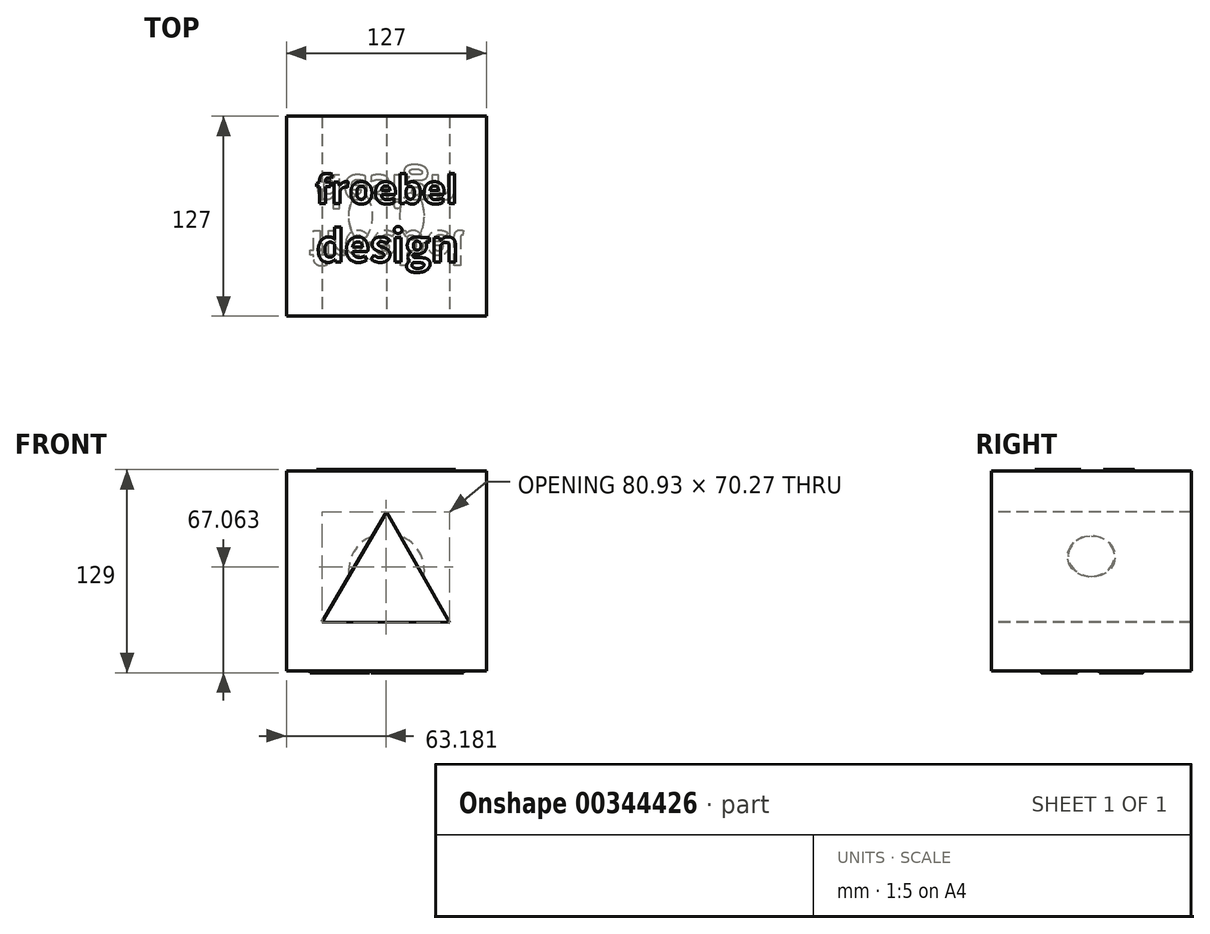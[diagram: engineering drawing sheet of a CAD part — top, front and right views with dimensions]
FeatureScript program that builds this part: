
annotation { "Feature Type Name" : "Feature", "Feature Type Description" : "" }
export const myFeature = defineFeature(function(context is Context, id is Id, definition is map)
    precondition{}
    {
        {
            var Q0;
            Q0=qCreatedBy(makeId("Top.planeOp"),FACE);
            var sketch = newSketch(context, id + "F0", { "sketchPlane" : qUnion([Q0])});
            skLineSegment(sketch, "E0.bottom", {"start": v(63.5, -63.5) * mm, "end": v(-63.5, -63.5) * mm});
            skLineSegment(sketch, "E0.top", {"start": v(63.5, 63.5) * mm, "end": v(-63.5, 63.5) * mm});
            skLineSegment(sketch, "E0.left", {"start": v(63.5, -63.5) * mm, "end": v(63.5, 63.5) * mm});
            skLineSegment(sketch, "E0.right", {"start": v(-63.5, -63.5) * mm, "end": v(-63.5, 63.5) * mm});
            skPoint(sketch, "E0.middle", {"position": v(0, 0) * mm});
            skSolve(sketch);
        }
        {
            var Q0;
            Q0 = qSketchRegion(id + "F0", true);
            extrude(context, id + "F1", {"entities" : qUnion([Q0]), "depth" : 63.5 * mm, "hasSecondDirection" : true, "secondDirectionOppositeDirection" : true, "secondDirectionDepth" : 63.5 * mm});
        }
        {
            var Q0;
            Q0=qCreatedBy(makeId("Front.planeOp"),FACE);
            var sketch = newSketch(context, id + "F2", { "sketchPlane" : qUnion([Q0])});
            skArc(sketch, "E1", {"start": v(0, 24.07) * mm, "mid": v(24.07, 0) * mm, "end": v(0, -24.07) * mm});
            skLineSegment(sketch, "E2", {"start": v(0, -24.07) * mm, "end": v(0, 24.07) * mm});
            skSolve(sketch);
        }
        {
            var Q0;
            Q0 = qSketchRegion(id + "F2", true);
            var Q1;
            Q1=sQuery(id+"F2.wireOp",EDGE,"E2");
            revolve(context, id + "F3", {"entities" : qUnion([Q0]), "axis" : qUnion([Q1]), "revolveType" : RevolveType.FULL});
        }
        {
            var Q0;
            Q0=makeQuery(id+"F1.opExtrude","SWEPT_FACE",FACE,{"disambiguationData":[OSD([sQuery(id+"F0.wireOp",EDGE,"E0.bottom")])]});
            var sketch = newSketch(context, id + "F4", { "sketchPlane" : qUnion([Q0])});
            skCircle(sketch, "E3.cCircle", {"center": v(-0.21, -9.03) * mm, "radius": 23.36 * mm, "construction": true});
            skLineSegment(sketch, "E3.0", {"start": v(0, 37.7) * mm, "end": v(40.15, -32.57) * mm});
            skLineSegment(sketch, "E3.1", {"start": v(40.15, -32.57) * mm, "end": v(-40.78, -32.2) * mm});
            skLineSegment(sketch, "E3.2", {"start": v(-40.78, -32.2) * mm, "end": v(0, 37.7) * mm});
            skPoint(sketch, "E3.0.midPoint", {"position": v(20.07, 2.56) * mm});
            skSolve(sketch);
        }
        {
            var Q0;
            Q0=makeQuery(id+"F4.imprint","IMPRINT",FACE,{"disambiguationData":[TD([[makeQuery(id+"F4.imprint","IMPRINT",EDGE,{"derivedFrom":sQuery(id+"F4.wireOp",EDGE,"E3.0")}),-1.0]])]});
            extrude(context, id + "F5", {"entities" : qUnion([Q0]), "operationType" : NewBodyOperationType.REMOVE, "endBound" : BoundingType.THROUGH_ALL, "oppositeDirection" : true, "depth" : 25.4 * mm});
        }
        {
            var Q0;
            Q0=qCreatedBy(makeId("Front.planeOp"),FACE);
            var sketch = newSketch(context, id + "F6", { "sketchPlane" : qUnion([Q0])});
            skLineSegment(sketch, "E4", {"start": v(0, 61.7) * mm, "end": v(0, -90.48) * mm});
            skSolve(sketch);
        }
        {
            var Q0;
            Q0=qCreatedBy(makeId("Front.planeOp"),FACE);
            var sketch = newSketch(context, id + "F7", { "sketchPlane" : qUnion([Q0])});
            skLineSegment(sketch, "E5", {"start": v(0, 0) * mm, "end": v(0, 95.52) * mm});
            skSolve(sketch);
        }
        {
            var Q0;
            Q0=makeQuery(id+"F1.opExtrude","CAP_FACE",FACE,{"disambiguationData":[OSD([sQuery(id+"F0.wireOp",EDGE,"E0.bottom"),sQuery(id+"F0.wireOp",EDGE,"E0.top"),sQuery(id+"F0.wireOp",EDGE,"E0.left"),sQuery(id+"F0.wireOp",EDGE,"E0.right")])],"isStart":false});
            var sketch = newSketch(context, id + "F8", { "sketchPlane" : qUnion([Q0])});
            skText(sketch, "E6", { "text": "froebel", "fontName": "OpenSans-Bold.ttf"});
            const initialGuessF8  = {"E6": [-0.045, 0.0079, 1, 0, 0.01817]};
            skSetInitialGuess(sketch, initialGuessF8);
            skSolve(sketch);
        }
        {
            var Q0;
            Q0=makeQuery(id+"F8.imprint","IMPRINT",FACE,{"disambiguationData":[TD([[makeQuery(id+"F8.imprint","IMPRINT",EDGE,{"derivedFrom":sQuery(id+"F8.wireOp",EDGE,"E6.sketch_text.stroke-0")}),1.0]])]});
            var sketch = newSketch(context, id + "F9", { "sketchPlane" : qUnion([Q0])});
            skText(sketch, "E7", { "text": "design", "fontName": "NotoSansCJKsc-Bold.otf"});
            const initialGuessF9  = {"E7": [-0.04464, -0.02906, 1, 0, 0.02]};
            skSetInitialGuess(sketch, initialGuessF9);
            skSolve(sketch);
        }
        {
            var Q0;
            Q0=makeQuery(id+"F1.opExtrude","CAP_FACE",FACE,{"disambiguationData":[OSD([sQuery(id+"F0.wireOp",EDGE,"E0.bottom"),sQuery(id+"F0.wireOp",EDGE,"E0.top"),sQuery(id+"F0.wireOp",EDGE,"E0.left"),sQuery(id+"F0.wireOp",EDGE,"E0.right")])],"isStart":true});
            var sketch = newSketch(context, id + "F10", { "sketchPlane" : qUnion([Q0])});
            skText(sketch, "E8", { "text": "froebel", "fontName": "NotoSansCJKsc-Bold.otf"});
            const initialGuessF10  = {"E8": [-0.0492, 0.0092, 1, 0, 0.02]};
            skSetInitialGuess(sketch, initialGuessF10);
            skSolve(sketch);
        }
        {
            var Q0;
            {var subQ0=sQuery(id+"F0.wireOp",EDGE,"E0.right");var subQ1=sQuery(id+"F0.wireOp",EDGE,"E0.left");var subQ2=sQuery(id+"F0.wireOp",EDGE,"E0.top");var subQ3=sQuery(id+"F0.wireOp",EDGE,"E0.bottom");Q0=makeQuery(id+"FUg0wyrOaobAqVz_3.boolean.opBoolean","SPLIT",FACE,{"disambiguationData":[TD([makeQuery(id+"FUg0wyrOaobAqVz_3.opExtrude","SWEPT_FACE",FACE,{"disambiguationData":[OSD([sQuery(id+"F10.wireOp",EDGE,"E8.sketch_text.stroke-0")])]})])],"derivedFrom":makeQuery(id+"F1.opExtrude","CAP_FACE",FACE,{"disambiguationData":[OSD([subQ3,subQ2,subQ1,subQ0])],"isStart":true})});}
            var sketch = newSketch(context, id + "F11", { "sketchPlane" : qUnion([Q0])});
            skText(sketch, "E9", { "text": "design", "fontName": "OpenSans-Bold.ttf"});
            const initialGuessF11  = {"E9": [-0.04515, -0.02609, 1, 0, 0.02]};
            skSetInitialGuess(sketch, initialGuessF11);
            skSolve(sketch);
        }
        {
            var Q0;
            Q0 = qSketchRegion(id + "F8", true);
            var Q1;
            Q1 = qSketchRegion(id + "F9", true);
            extrude(context, id + "F12", {"entities" : qUnion([Q0, Q1]), "operationType" : NewBodyOperationType.ADD, "depth" : 1 * mm, "offsetDistance" : 25 * mm});
        }
        {
            var Q0;
            Q0 = qSketchRegion(id + "F10", true);
            var Q1;
            Q1 = qSketchRegion(id + "F11", true);
            extrude(context, id + "F13", {"entities" : qUnion([Q0, Q1]), "operationType" : NewBodyOperationType.ADD, "depth" : 1 * mm, "offsetDistance" : 25 * mm});
        }
    });
